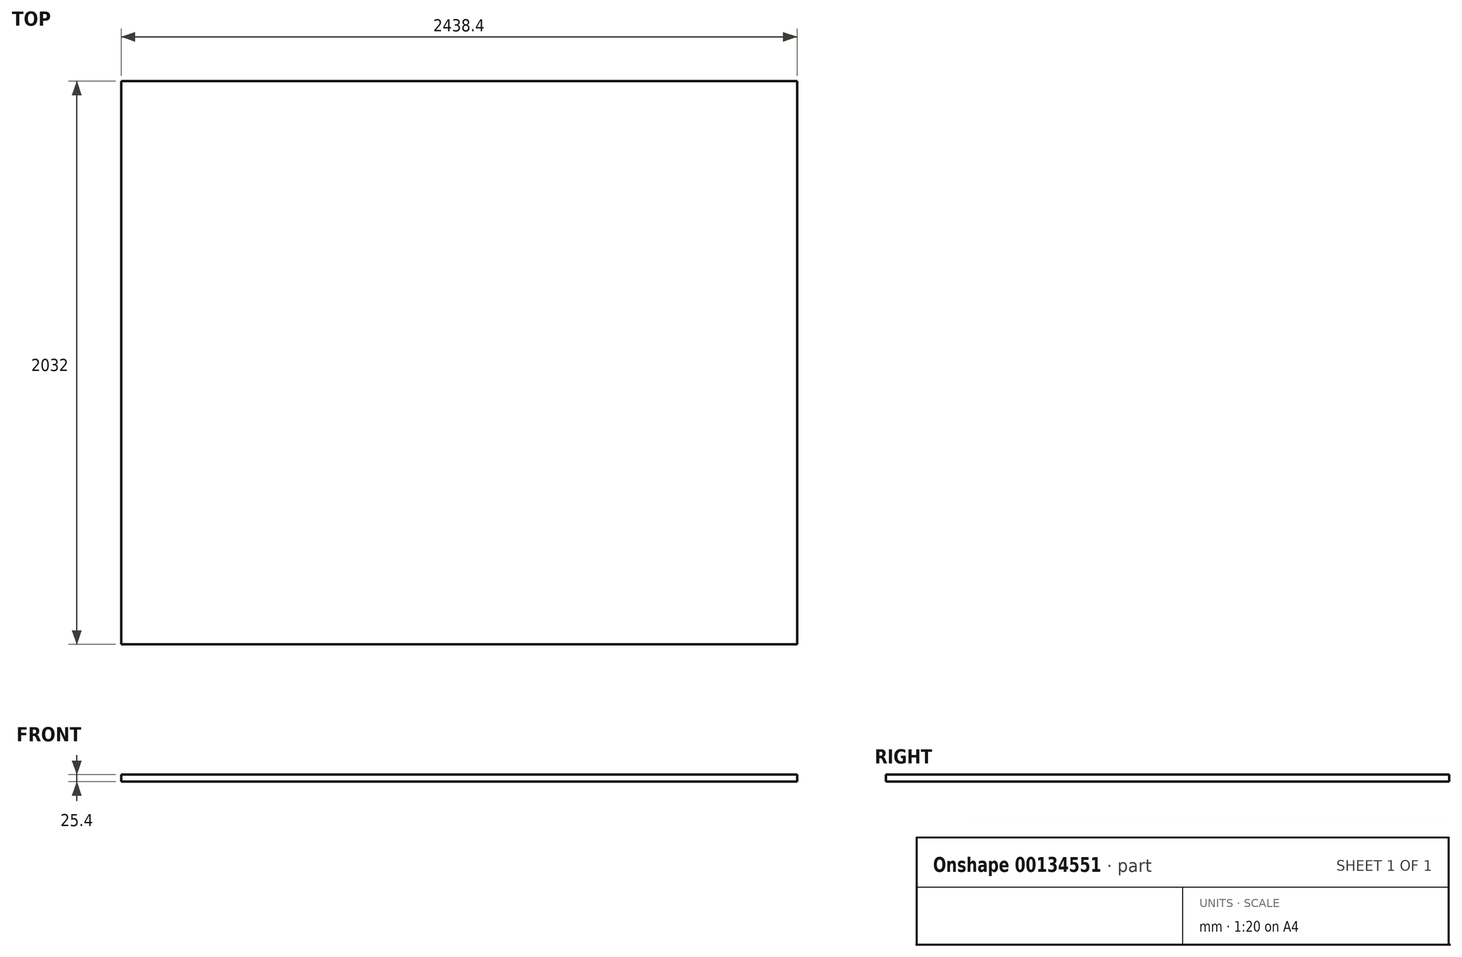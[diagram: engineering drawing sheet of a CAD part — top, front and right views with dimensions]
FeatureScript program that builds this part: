
annotation { "Feature Type Name" : "Feature", "Feature Type Description" : "" }
export const myFeature = defineFeature(function(context is Context, id is Id, definition is map)
    precondition{}
    {
        {
            var Q0;
            Q0=qCreatedBy(makeId("Top.planeOp"),FACE);
            var sketch = newSketch(context, id + "F0", { "sketchPlane" : qUnion([Q0])});
            skLineSegment(sketch, "E0", {"start": v(-53.62, 60.5) * mm, "end": v(2384.78, 60.5) * mm});
            skLineSegment(sketch, "E1", {"start": v(2384.78, 60.5) * mm, "end": v(2384.78, -1971.5) * mm});
            skLineSegment(sketch, "E2", {"start": v(2384.78, -1971.5) * mm, "end": v(-53.62, -1971.5) * mm});
            skLineSegment(sketch, "E3", {"start": v(-53.62, -1971.5) * mm, "end": v(-53.62, 60.5) * mm});
            skSolve(sketch);
        }
        {
            var Q0;
            Q0=makeQuery(id+"F0.imprint","IMPRINT",FACE,{"disambiguationData":[TD([[makeQuery(id+"F0.imprint","IMPRINT",EDGE,{"derivedFrom":sQuery(id+"F0.wireOp",EDGE,"E0")}),-1.0]])]});
            extrude(context, id + "F1", {"entities" : qUnion([Q0]), "depth" : 25.4 * mm});
        }
    });
